# Revit family: Sink-Vessel-Lavatory-KOHLER-Purist_Wading_Pool-K-2314_1
name_source: partatom
category: Plumbing Fixtures
revit_build: Autodesk Revit 2017 (Build: 20160225_1515(x64)
units: mm (PartAtom-declared; Revit-internal decimal feet)

## family parameters
Cut with Voids When Loaded = No
Host = Face
OmniClass Number = 23.31.13.00
OmniClass Title = Sinks
Part Type = Normal
Room Calculation Point = No
Round Connector Dimension = Use Diameter
Shared = No

## types (6) — shared parameters
ADA Compliant = Yes
Assembly Code = D2010400
CW Connection = No
Cold Water Inlet = Cold Water Inlet
Date Modified = 07/17/2020
Default Elevation = 36"
Drain Included = No
HW Connection = No
Height = 4 1/8"
Hot Water Inlet = Hot Water Inlet
Length = 23 15/16"
Manufacturer = KOHLER Co.
Master Format 2014 = 22 41 16
Master Format 2014 Name = Residential Lavatories and Sinks
Material = Fireclay
Product Documentation Link = https://www.us.kohler.com
Product Name = Purist Wading Pool
Product Page URL = http://www.us.kohler.com
URL = https://www.us.kohler.com
Vent Connection = No
Waste Connection = Yes
Waste Water Outlet = Waste Water Outlet
WaterSense Certified = No
Width = 24 1/4"

## per-type parameters (varying)
| type | 1 Hole | 3 Hole | Description | Faucet Hole Spacing | Finish | Model | No Hole | Type |
| No Hole, 0-White | No | No | Above-counter/wall-mount vessel bathroom sink | 0" | KOHLER-Fireclay-0-White | K-2314-0 | Yes | 1 |
| No Hole, 96-Biscuit | No | No | Above-counter/wall-mount vessel bathroom sink | 0" | KOHLER-Fireclay-96-Biscuit | K-2314-96 | Yes | 2 |
| Single Hole, 0-White | Yes | No | Fireclay vessel bathroom sink with single faucet hole | 0" | KOHLER-Fireclay-0-White | K-2314-1-0 | No | 3 |
| Single Hole, 96-Biscuit | Yes | No | Fireclay vessel bathroom sink with single faucet hole | 0" | KOHLER-Fireclay-96-Biscuit | K-2314-1-96 | No | 4 |
| 8" Widespread Holes, 0-White | No | Yes | Fireclay vessel bathroom sink with 8inch widespread faucet holes | 8" | KOHLER-Fireclay-0-White | K-2314-8-0 | No | 5 |
| 8" Widespread Holes, 96-Biscuit | No | Yes | Fireclay vessel bathroom sink with 8inch widespread faucet holes | 8" | KOHLER-Fireclay-96-Biscuit | K-2314-8-96 | No | 6 |

## geometry (parser evidence)
native form markers: Sweep x4
no freeform markers — native parametric forms only
